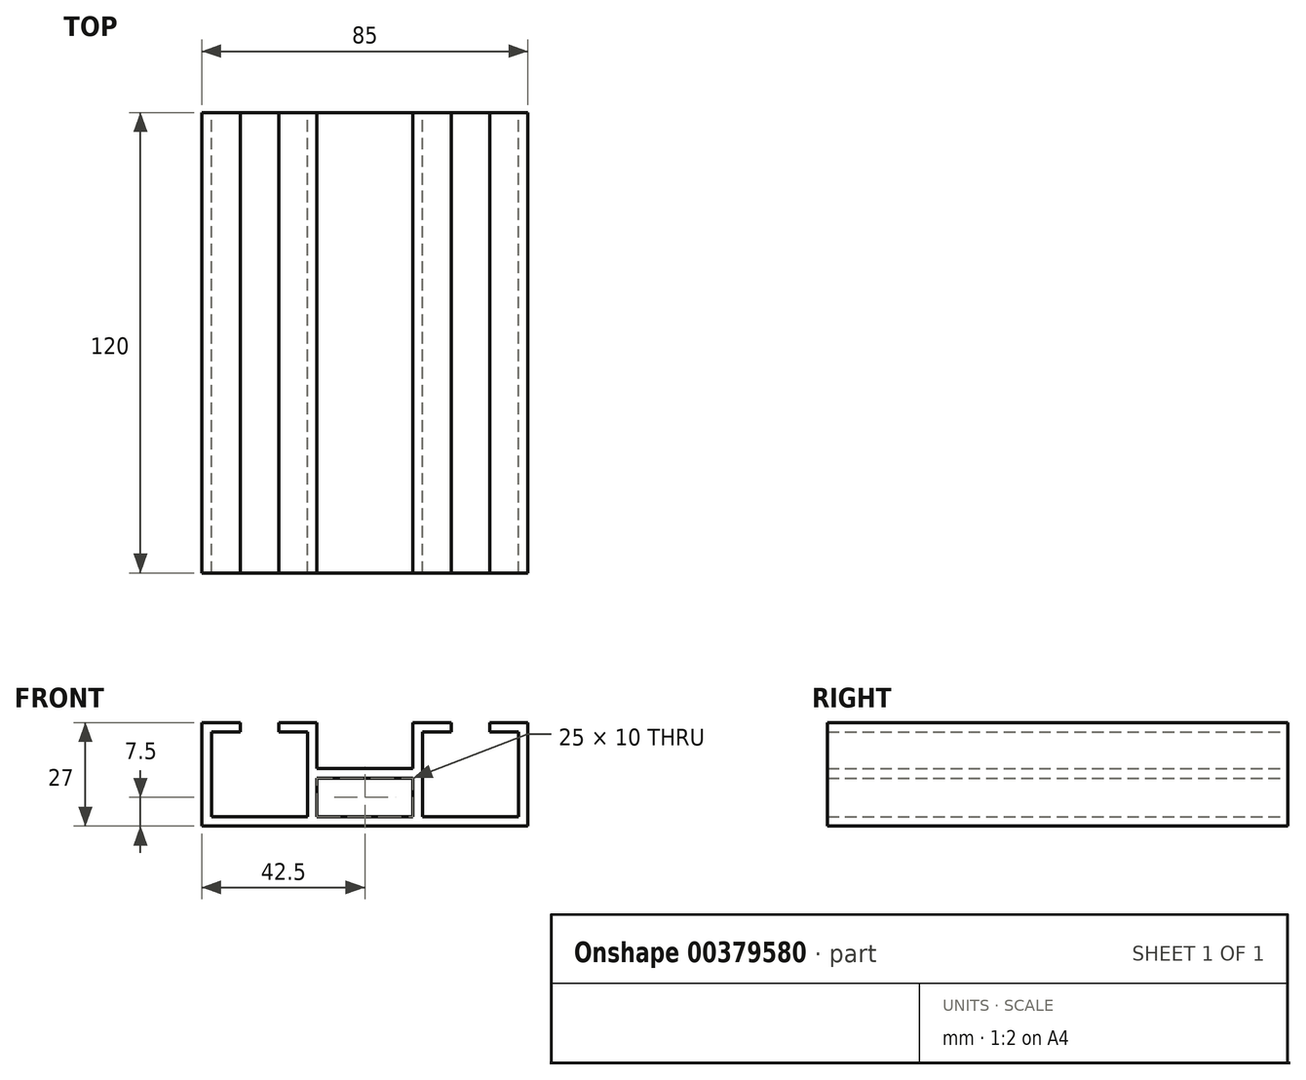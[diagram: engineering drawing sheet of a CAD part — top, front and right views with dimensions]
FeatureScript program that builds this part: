
annotation { "Feature Type Name" : "Feature", "Feature Type Description" : "" }
export const myFeature = defineFeature(function(context is Context, id is Id, definition is map)
    precondition{}
    {
        {
            var Q0;
            Q0=qCreatedBy(makeId("Front.planeOp"),FACE);
            var sketch = newSketch(context, id + "F0", { "sketchPlane" : qUnion([Q0])});
            skLineSegment(sketch, "E0.bottom", {"start": v(42.5, 17.5) * mm, "end": v(-42.5, 17.5) * mm});
            skLineSegment(sketch, "E0.top", {"start": v(42.5, -17.5) * mm, "end": v(-42.5, -17.5) * mm});
            skLineSegment(sketch, "E0.left", {"start": v(42.5, 17.5) * mm, "end": v(42.5, -17.5) * mm});
            skLineSegment(sketch, "E0.right", {"start": v(-42.5, 17.5) * mm, "end": v(-42.5, -17.5) * mm});
            skPoint(sketch, "E0.middle", {"position": v(0, 0) * mm});
            skLineSegment(sketch, "E1.bottom", {"start": v(-15, 7) * mm, "end": v(-40, 7) * mm});
            skLineSegment(sketch, "E1.top", {"start": v(-15, -15) * mm, "end": v(-40, -15) * mm});
            skLineSegment(sketch, "E1.left", {"start": v(-15, 7) * mm, "end": v(-15, -15) * mm});
            skLineSegment(sketch, "E1.right", {"start": v(-40, 7) * mm, "end": v(-40, -15) * mm});
            skPoint(sketch, "E1.middle", {"position": v(-27.5, -4) * mm});
            skLineSegment(sketch, "E2.MirrorCS", {"start": v(15, 7) * mm, "end": v(40, 7) * mm});
            skLineSegment(sketch, "E3.MirrorCS", {"start": v(40, 7) * mm, "end": v(40, -15) * mm});
            skLineSegment(sketch, "E4.MirrorCS", {"start": v(15, -15) * mm, "end": v(40, -15) * mm});
            skLineSegment(sketch, "E5.MirrorCS", {"start": v(15, 7) * mm, "end": v(15, -15) * mm});
            skPoint(sketch, "E6.MirrorP", {"position": v(27.5, -4) * mm});
            skLineSegment(sketch, "E7.bottom", {"start": v(12.5, -5) * mm, "end": v(-12.5, -5) * mm});
            skLineSegment(sketch, "E7.top", {"start": v(12.5, -15) * mm, "end": v(-12.5, -15) * mm});
            skLineSegment(sketch, "E7.left", {"start": v(12.5, -5) * mm, "end": v(12.5, -15) * mm});
            skLineSegment(sketch, "E7.right", {"start": v(-12.5, -5) * mm, "end": v(-12.5, -15) * mm});
            skPoint(sketch, "E7.middle", {"position": v(0, -10) * mm});
            skLineSegment(sketch, "E8.bottom", {"start": v(12.5, 17.5) * mm, "end": v(-12.5, 17.5) * mm});
            skLineSegment(sketch, "E8.top", {"start": v(12.5, -2.5) * mm, "end": v(-12.5, -2.5) * mm});
            skLineSegment(sketch, "E8.left", {"start": v(12.5, 17.5) * mm, "end": v(12.5, -2.5) * mm});
            skLineSegment(sketch, "E8.right", {"start": v(-12.5, 17.5) * mm, "end": v(-12.5, -2.5) * mm});
            skPoint(sketch, "E8.middle", {"position": v(0, 7.5) * mm});
            skLineSegment(sketch, "E9", {"start": v(-42.5, 9.5) * mm, "end": v(-32.5, 9.5) * mm});
            skLineSegment(sketch, "E10", {"start": v(-32.5, 9.5) * mm, "end": v(-32.5, 7) * mm});
            skLineSegment(sketch, "E11", {"start": v(-12.5, 9.5) * mm, "end": v(-22.5, 9.5) * mm});
            skLineSegment(sketch, "E12", {"start": v(-22.5, 9.5) * mm, "end": v(-22.5, 7) * mm});
            skLineSegment(sketch, "E13.MirrorCS", {"start": v(12.5, 9.5) * mm, "end": v(22.5, 9.5) * mm});
            skLineSegment(sketch, "E14.MirrorCS", {"start": v(22.5, 9.5) * mm, "end": v(22.5, 7) * mm});
            skLineSegment(sketch, "E15.MirrorCS", {"start": v(32.5, 9.5) * mm, "end": v(32.5, 7) * mm});
            skLineSegment(sketch, "E16.MirrorCS", {"start": v(42.5, 9.5) * mm, "end": v(32.5, 9.5) * mm});
            skLineSegment(sketch, "E17", {"start": v(-32.5, 7) * mm, "end": v(-22.5, 7) * mm});
            skLineSegment(sketch, "E18", {"start": v(22.5, 7) * mm, "end": v(32.5, 7) * mm});
            skSolve(sketch);
        }
        {
            var Q0;
            {var subQ9=sQuery(id+"F0.wireOp",EDGE,"E0.top");Q0=makeQuery(id+"F0.imprint","IMPRINT",FACE,{"disambiguationData":[TD([[makeQuery(id+"F0.imprint","IMPRINT",EDGE,{"derivedFrom":subQ9}),-1.0]])]});}
            extrude(context, id + "F1", {"entities" : qUnion([Q0]), "endBound" : BoundingType.SYMMETRIC, "depth" : 120 * mm});
        }
    });
